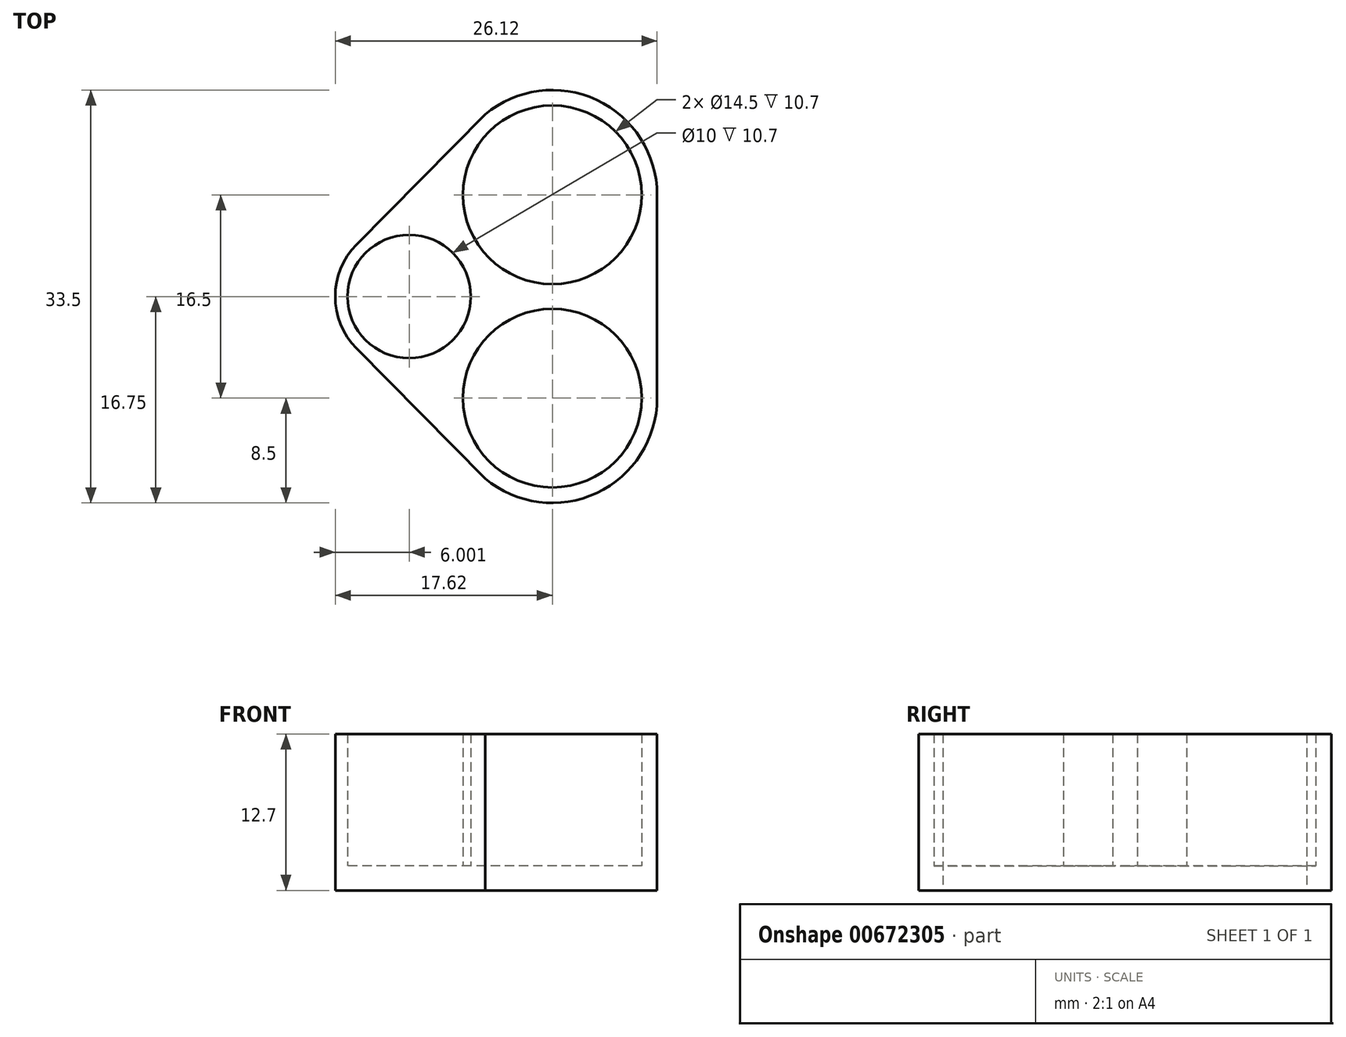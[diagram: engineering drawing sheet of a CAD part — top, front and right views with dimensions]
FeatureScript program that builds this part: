
annotation { "Feature Type Name" : "Feature", "Feature Type Description" : "" }
export const myFeature = defineFeature(function(context is Context, id is Id, definition is map)
    precondition{}
    {
        {
            var Q0;
            Q0=qCreatedBy(makeId("Top.planeOp"),FACE);
            var sketch = newSketch(context, id + "F0", { "sketchPlane" : qUnion([Q0])});
            skCircle(sketch, "E0", {"center": v(0, 0) * mm, "radius": 7.25 * mm});
            skCircle(sketch, "E1", {"center": v(0, 16.5) * mm, "radius": 7.25 * mm});
            skCircle(sketch, "E2", {"center": v(-11.62, 8.25) * mm, "radius": 5 * mm});
            skArc(sketch, "E3", {"start": v(8.5, 16.5) * mm, "mid": v(2.86, 24.5) * mm, "end": v(-6.58, 21.88) * mm});
            skArc(sketch, "E4", {"start": v(-6.58, -5.38) * mm, "mid": v(2.86, -8) * mm, "end": v(8.5, 0) * mm});
            skArc(sketch, "E5", {"start": v(-15.89, 12.47) * mm, "mid": v(-17.62, 8.25) * mm, "end": v(-15.89, 4.03) * mm});
            skLineSegment(sketch, "E6", {"start": v(8.5, 0) * mm, "end": v(8.5, 16.5) * mm});
            skLineSegment(sketch, "E7", {"start": v(-5.46, 23.02) * mm, "end": v(-15.89, 12.47) * mm});
            skLineSegment(sketch, "E8", {"start": v(-5.45, -6.52) * mm, "end": v(-15.89, 4.03) * mm});
            skSolve(sketch);
        }
        {
            var Q0;
            Q0=makeQuery(id+"F0.imprint","IMPRINT",FACE,{"disambiguationData":[TD([[makeQuery(id+"F0.imprint","IMPRINT",EDGE,{"derivedFrom":sQuery(id+"F0.wireOp",EDGE,"E0")}),-1.0]])]});
            extrude(context, id + "F1", {"entities" : qUnion([Q0]), "depth" : 12.7 * mm, "offsetDistance" : 25.4 * mm});
        }
        {
            var Q0;
            Q0=makeQuery(id+"F0.imprint","IMPRINT",FACE,{"disambiguationData":[TD([[makeQuery(id+"F0.imprint","IMPRINT",EDGE,{"derivedFrom":sQuery(id+"F0.wireOp",EDGE,"E0")}),-1.0]])]});
            var Q1;
            Q1=makeQuery(id+"F0.imprint","IMPRINT",FACE,{"disambiguationData":[TD([[makeQuery(id+"F0.imprint","IMPRINT",EDGE,{"derivedFrom":sQuery(id+"F0.wireOp",EDGE,"E1")}),1.0]])]});
            var Q2;
            Q2=makeQuery(id+"F0.imprint","IMPRINT",FACE,{"disambiguationData":[TD([[makeQuery(id+"F0.imprint","IMPRINT",EDGE,{"derivedFrom":sQuery(id+"F0.wireOp",EDGE,"E0")}),1.0]])]});
            var Q3;
            Q3=makeQuery(id+"F0.imprint","IMPRINT",FACE,{"disambiguationData":[TD([[makeQuery(id+"F0.imprint","IMPRINT",EDGE,{"derivedFrom":sQuery(id+"F0.wireOp",EDGE,"E2")}),1.0]])]});
            extrude(context, id + "F2", {"entities" : qUnion([Q0, Q1, Q2, Q3]), "operationType" : NewBodyOperationType.ADD, "depth" : 2 * mm, "offsetDistance" : 25.4 * mm});
        }
    });
